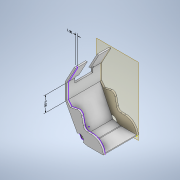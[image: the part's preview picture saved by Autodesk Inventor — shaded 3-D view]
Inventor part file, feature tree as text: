
AUTODESK INVENTOR PART (.ipt)
format: ipt  version: 2021 (Build 250183000, 183)  size: 224,256 bytes
history: native  units: in
note: dims shown in document units (in); Inventor stores cm internally (conversion verified against a paired STEP export)
features: sketch x8, extrude x6, other x3, plane x1
ambient origin geometry x8: Origin, YZ Plane, XZ Plane, XY Plane, X Axis, Y Axis, Z Axis, Center Point
bodies: Solid1 (feature_tree)
feature tree (18):
  other  "Annotations"
  sketch  "Sketch1"  dims[d63=0.5in d64=0.5in]
  extrude  "Extrusion1"  Depth=0.5in
  extrude  "Extrusion2"  Depth=0.5in
  plane  "Work Plane3"
  sketch  "Sketch5"  dims[d68=0.5in d69=18.5in d70=0.0in]
  sketch  "Sketch6"  dims[d71=1.0in d72=0.0in d73=-18.5in]
  extrude  "Extrusion3"  Depth=18.5in TaperAngle=0.0deg
  extrude  "Extrusion4"  [1 undecoded]
  extrude  "Extrusion6"  Depth=9.0in
  extrude  "Extrusion7"  Depth=5.25in
  sketch  "Sketch4"  dims[d65=0.5in d66=0.5in]
  sketch  "Sketch7"  dims[d74=1.0in d75=0.0in d77=9.0in]
  sketch  "Sketch8"  dims[d78=23.5in d80=5.25in]
  sketch  "Sketch11"  dims[d81=5.25in]
  sketch  "Sketch12"  dims[d82=20.0in d83=10.5in d84=1.0in d85=1.875in d86=1.875in d87=36.0in d88=0.0in d92=4.75in d93=1.0in d94=0.0in d95=4.75in d96=1.0in d97=0.0in d57=1.0004in d76=9.0in d24=0.5in d25=0.0344in d26=0.5in d27=0.0344in]
  other  "Linear Dimension 1"
  other  "Linear Dimension 2"
note: 1 required parameter value undecoded (feature->parameter linkage not recoverable at this tier; creation-order binding heuristic only, values carry confidence <= 0.55)
